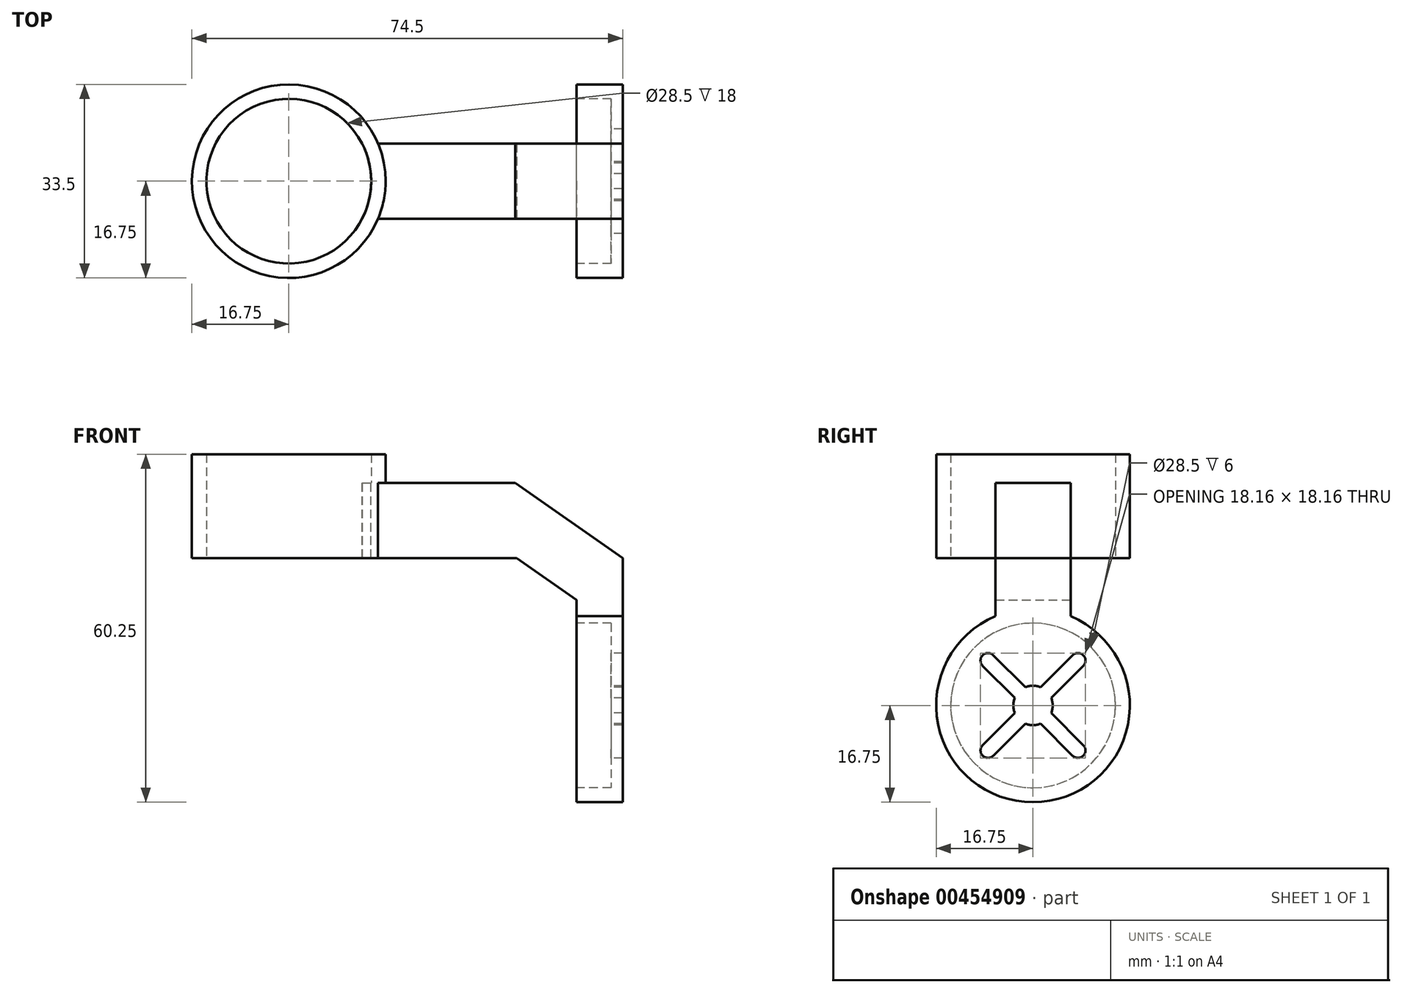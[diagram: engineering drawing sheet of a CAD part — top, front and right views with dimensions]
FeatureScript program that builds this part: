
annotation { "Feature Type Name" : "Feature", "Feature Type Description" : "" }
export const myFeature = defineFeature(function(context is Context, id is Id, definition is map)
    precondition{}
    {
        {
            var Q0;
            Q0=qCreatedBy(makeId("Top.planeOp"),FACE);
            var sketch = newSketch(context, id + "F0", { "sketchPlane" : qUnion([Q0])});
            skCircle(sketch, "E0", {"center": v(0, 0) * mm, "radius": 14.25 * mm});
            skCircle(sketch, "E1", {"center": v(0, 0) * mm, "radius": 16.75 * mm});
            skSolve(sketch);
        }
        {
            var Q0;
            Q0 = qSketchRegion(id + "F0", true);
            extrude(context, id + "F1", {"entities" : qUnion([Q0]), "depth" : 18 * mm});
        }
        {
            var Q0;
            Q0=qCreatedBy(makeId("Front.planeOp"),FACE);
            var sketch = newSketch(context, id + "F2", { "sketchPlane" : qUnion([Q0])});
            skLineSegment(sketch, "E2", {"start": v(39.05, 13) * mm, "end": v(39.15, 13) * mm});
            skLineSegment(sketch, "E3", {"start": v(44.75, 0) * mm, "end": v(44.75, -25.5) * mm});
            skPoint(sketch, "E4.orphan", {"position": v(57.75, 0) * mm});
            skLineSegment(sketch, "E5", {"start": v(57.75, 0) * mm, "end": v(39.15, 13) * mm});
            skLineSegment(sketch, "E6", {"start": v(44.75, -25.5) * mm, "end": v(57.75, -25.5) * mm});
            skLineSegment(sketch, "E7", {"start": v(57.75, -25.5) * mm, "end": v(57.75, 0) * mm});
            skPoint(sketch, "E8.orphan", {"position": v(57.75, 13) * mm});
            skLineSegment(sketch, "E9", {"start": v(39.05, 13) * mm, "end": v(9.9, 13) * mm});
            skLineSegment(sketch, "E10", {"start": v(9.9, 13) * mm, "end": v(9.9, 0) * mm});
            skLineSegment(sketch, "E11", {"start": v(44.75, 0) * mm, "end": v(9.9, 0) * mm});
            skSolve(sketch);
        }
        {
            var Q0;
            Q0 = qSketchRegion(id + "F2", true);
            extrude(context, id + "F3", {"entities" : qUnion([Q0]), "operationType" : NewBodyOperationType.ADD, "depth" : 13 / 2 * mm, "hasSecondDirection" : true, "secondDirectionOppositeDirection" : true, "secondDirectionDepth" : 6.5 * mm});
        }
        {
            var Q0;
            Q0=makeQuery(id+"F1.opExtrude","CAP_FACE",FACE,{"disambiguationData":[OSD([sQuery(id+"F0.wireOp",EDGE,"E0"),sQuery(id+"F0.wireOp",EDGE,"E1")])],"isStart":false});
            var sketch = newSketch(context, id + "F4", { "sketchPlane" : qUnion([Q0])});
            skCircle(sketch, "E12", {"center": v(0, 0) * mm, "radius": 14.24 * mm});
            skSolve(sketch);
        }
        {
            var Q0;
            Q0=makeQuery(id+"F4.imprint","IMPRINT",FACE,{"disambiguationData":[TD([[makeQuery(id+"F4.imprint","IMPRINT",EDGE,{"derivedFrom":sQuery(id+"F4.wireOp",EDGE,"E12")}),1.0]])]});
            extrude(context, id + "F5", {"entities" : qUnion([Q0]), "operationType" : NewBodyOperationType.REMOVE, "oppositeDirection" : true, "depth" : 25 * mm});
        }
        {
            var Q0;
            Q0=makeQuery(id+"F3.opExtrude","SWEPT_FACE",FACE,{"disambiguationData":[OSD([sQuery(id+"F2.wireOp",EDGE,"E7")])]});
            var sketch = newSketch(context, id + "F6", { "sketchPlane" : qUnion([Q0])});
            skCircle(sketch, "E13", {"center": v(0, -25.5) * mm, "radius": 16.75 * mm});
            skLineSegment(sketch, "E14", {"start": v(-16.75, 0) * mm, "end": v(-16.75, 18) * mm, "construction": true});
            skLineSegment(sketch, "E15", {"start": v(-16.75, 0) * mm, "end": v(-16.75, -40.9) * mm, "construction": true});
            skSolve(sketch);
        }
        {
            var Q0;
            Q0 = qSketchRegion(id + "F6", true);
            extrude(context, id + "F7", {"entities" : qUnion([Q0]), "operationType" : NewBodyOperationType.ADD, "oppositeDirection" : true, "depth" : 8 * mm});
        }
        {
            var Q0;
            {var subQ0=sQuery(id+"F2.wireOp",EDGE,"ThWkjC9a-3eqL-S6FN-Etdi-DtM8RTVKEJxe");var subQ1=sQuery(id+"F2.wireOp",EDGE,"YqEWwE9g-cm7q-8xzn-DUqV-dWurj4cPjtdj");var subQ2=sQuery(id+"F0.wireOp",EDGE,"E1");var subQ3=sQuery(id+"F2.wireOp",EDGE,"E9");var subQ4=sQuery(id+"F2.wireOp",EDGE,"E2");var subQ5=sQuery(id+"F2.wireOp",EDGE,"E3");var subQ6=sQuery(id+"F2.wireOp",EDGE,"E5");var subQ7=sQuery(id+"F2.wireOp",EDGE,"E6");var subQ8=sQuery(id+"F2.wireOp",EDGE,"E7");Q0=makeQuery(id+"F3.boolean.opBoolean","SPLIT",FACE,{"disambiguationData":[TD([makeQuery(id+"F1.opExtrude","SWEPT_FACE",FACE,{"disambiguationData":[OSD([subQ2])]})])],"derivedFrom":makeQuery(id+"F3.opExtrude","CAP_FACE",FACE,{"disambiguationData":[OSD([subQ1,subQ4,subQ5,subQ6,subQ7,subQ8,subQ3,sQuery(id+"F2.wireOp",EDGE,"E10"),subQ0])],"isStart":false})});}
            var sketch = newSketch(context, id + "F8", { "sketchPlane" : qUnion([Q0])});
            skLineSegment(sketch, "E16", {"start": v(49.75, -25.5) * mm, "end": v(44.75, -25.5) * mm});
            skLineSegment(sketch, "E17", {"start": v(44.75, -25.5) * mm, "end": v(44.75, -6.08) * mm});
            skLineSegment(sketch, "E18", {"start": v(44.75, -6.08) * mm, "end": v(49.75, -10.06) * mm});
            skLineSegment(sketch, "E19", {"start": v(49.75, -10.06) * mm, "end": v(49.75, -10.06) * mm});
            skSolve(sketch);
        }
        {
            var Q0;
            Q0 = qSketchRegion(id + "F8", true);
            var Q1;
            Q1=makeQuery(id+"F8.imprint","IMPRINT",FACE,{"disambiguationData":[TD([[makeQuery(id+"F8.imprint","IMPRINT",EDGE,{"derivedFrom":sQuery(id+"F8.wireOp",EDGE,"E16")}),1.0]])]});
            extrude(context, id + "F9", {"entities" : qUnion([Q0, Q1]), "operationType" : NewBodyOperationType.REMOVE, "oppositeDirection" : true, "depth" : 25 * mm});
        }
        {
            var Q0;
            {var subQ0=sQuery(id+"F6.wireOp",EDGE,"E13");Q0=makeQuery(id+"F9.boolean.opBoolean","MERGE",FACE,{"derivedFrom":[makeQuery(id+"F7.opExtrude","CAP_FACE",FACE,{"disambiguationData":[OSD([subQ0])],"isStart":false}),makeQuery(id+"F9.opExtrude","SWEPT_FACE",FACE,{"disambiguationData":[OSD([sQuery(id+"F2.wireOp",EDGE,"E2"),sQuery(id+"F2.wireOp",EDGE,"E3"),sQuery(id+"F2.wireOp",EDGE,"E5"),sQuery(id+"F2.wireOp",EDGE,"E6"),sQuery(id+"F2.wireOp",EDGE,"E7"),sQuery(id+"F2.wireOp",EDGE,"E9"),sQuery(id+"F2.wireOp",EDGE,"E10"),sQuery(id+"F2.wireOp",EDGE,"E11"),subQ0])]})]});}
            var sketch = newSketch(context, id + "F10", { "sketchPlane" : qUnion([Q0])});
            skCircle(sketch, "E20", {"center": v(0, -25.5) * mm, "radius": 14.25 * mm});
            skSolve(sketch);
        }
        {
            var Q0;
            Q0 = qSketchRegion(id + "F10", true);
            extrude(context, id + "F11", {"entities" : qUnion([Q0]), "operationType" : NewBodyOperationType.REMOVE, "oppositeDirection" : true, "depth" : 6 * mm, "hasSecondDirection" : true, "secondDirectionOppositeDirection" : false, "secondDirectionDepth" : 25 * mm});
        }
        {
            var Q0;
            {var subQ0=sQuery(id+"F2.wireOp",EDGE,"E9");var subQ1=sQuery(id+"F2.wireOp",EDGE,"E2");var subQ2=sQuery(id+"F0.wireOp",EDGE,"E1");var subQ3=sQuery(id+"F2.wireOp",EDGE,"E3");var subQ4=sQuery(id+"F2.wireOp",EDGE,"E5");var subQ5=sQuery(id+"F2.wireOp",EDGE,"E6");var subQ6=sQuery(id+"F2.wireOp",EDGE,"E7");var subQ7=sQuery(id+"F2.wireOp",EDGE,"E11");Q0=makeQuery(id+"F3.boolean.opBoolean","SPLIT",FACE,{"disambiguationData":[TD([makeQuery(id+"F1.opExtrude","SWEPT_FACE",FACE,{"disambiguationData":[OSD([subQ2])]})])],"derivedFrom":makeQuery(id+"F3.opExtrude","CAP_FACE",FACE,{"disambiguationData":[OSD([subQ1,subQ3,subQ4,subQ5,subQ6,subQ0,sQuery(id+"F2.wireOp",EDGE,"E10"),subQ7])],"isStart":false})});}
            var sketch = newSketch(context, id + "F12", { "sketchPlane" : qUnion([Q0])});
            skLineSegment(sketch, "E21", {"start": v(49.75, -7.23) * mm, "end": v(39.41, 0) * mm});
            skLineSegment(sketch, "E22", {"start": v(49.75, -7.23) * mm, "end": v(49.75, 0) * mm});
            skLineSegment(sketch, "E23", {"start": v(49.75, 0) * mm, "end": v(39.41, 0) * mm});
            skSolve(sketch);
        }
        {
            var Q0;
            Q0 = qSketchRegion(id + "F12", true);
            extrude(context, id + "F13", {"entities" : qUnion([Q0]), "operationType" : NewBodyOperationType.ADD, "oppositeDirection" : true, "depth" : 13 * mm});
        }
        {
            var Q0;
            {var subQ0=sQuery(id+"F2.wireOp",EDGE,"E9");var subQ1=sQuery(id+"F2.wireOp",EDGE,"E2");var subQ2=sQuery(id+"F0.wireOp",EDGE,"E1");var subQ3=sQuery(id+"F2.wireOp",EDGE,"E3");var subQ4=sQuery(id+"F2.wireOp",EDGE,"E5");var subQ5=sQuery(id+"F2.wireOp",EDGE,"E6");var subQ6=sQuery(id+"F2.wireOp",EDGE,"E7");var subQ7=sQuery(id+"F2.wireOp",EDGE,"E11");Q0=makeQuery(id+"F13.boolean.opBoolean","MERGE",FACE,{"derivedFrom":[makeQuery(id+"F3.boolean.opBoolean","SPLIT",FACE,{"disambiguationData":[TD([makeQuery(id+"F1.opExtrude","SWEPT_FACE",FACE,{"disambiguationData":[OSD([subQ2])]})])],"derivedFrom":makeQuery(id+"F3.opExtrude","CAP_FACE",FACE,{"disambiguationData":[OSD([subQ1,subQ3,subQ4,subQ5,subQ6,subQ0,sQuery(id+"F2.wireOp",EDGE,"E10"),subQ7])],"isStart":true})}),makeQuery(id+"F13.opExtrude","CAP_FACE",FACE,{"disambiguationData":[OSD([sQuery(id+"F12.wireOp",EDGE,"E21"),sQuery(id+"F12.wireOp",EDGE,"E22"),sQuery(id+"F12.wireOp",EDGE,"E23")])],"isStart":false})]});}
            var sketch = newSketch(context, id + "F14", { "sketchPlane" : qUnion([Q0])});
            skLineSegment(sketch, "E24", {"start": v(-49.75, -7.23) * mm, "end": v(-49.75, -10.06) * mm});
            skLineSegment(sketch, "E25", {"start": v(-49.75, -7.23) * mm, "end": v(-44.75, -3.73) * mm});
            skLineSegment(sketch, "E26", {"start": v(-49.75, -10.06) * mm, "end": v(-35.23, -9.45) * mm});
            skLineSegment(sketch, "E27", {"start": v(-35.23, -9.45) * mm, "end": v(-44.75, -3.73) * mm});
            skSolve(sketch);
        }
        {
            var Q0;
            Q0 = qSketchRegion(id + "F14", true);
            extrude(context, id + "F15", {"entities" : qUnion([Q0]), "operationType" : NewBodyOperationType.REMOVE, "oppositeDirection" : true, "depth" : 25 * mm});
        }
        {
            var Q0;
            Q0=makeQuery(id+"F11.boolean.opBoolean","COPY",FACE,{"derivedFrom":makeQuery(id+"F11.opExtrude","CAP_FACE",FACE,{"disambiguationData":[OSD([sQuery(id+"F10.wireOp",EDGE,"E20")])],"isStart":false})});
            var sketch = newSketch(context, id + "F16", { "sketchPlane" : qUnion([Q0])});
            skLineSegment(sketch, "E28", {"start": v(0, -25.5) * mm, "end": v(-14.25, -25.5) * mm, "construction": true});
            skPoint(sketch, "E29", {"position": v(-7.78, -17.72) * mm});
            skPoint(sketch, "E30", {"position": v(-2.23, -23.27) * mm});
            skArc(sketch, "E31.0.endCap", {"start": v(-8.7, -18.64) * mm, "mid": v(-8.7, -16.8) * mm, "end": v(-6.86, -16.8) * mm});
            skLineSegment(sketch, "E31.0.left", {"start": v(-3.15, -24.19) * mm, "end": v(-8.7, -18.64) * mm});
            skLineSegment(sketch, "E31.0.right", {"start": v(-1.31, -22.35) * mm, "end": v(-6.86, -16.8) * mm});
            skArc(sketch, "E32.MirrorCS", {"start": v(-6.86, -16.8) * mm, "mid": v(-8.7, -16.8) * mm, "end": v(-8.7, -18.64) * mm});
            skLineSegment(sketch, "E33.MirrorCS", {"start": v(0, -25.5) * mm, "end": v(-9.48, -25.5) * mm, "construction": true});
            skArc(sketch, "E34.MirrorCS", {"start": v(8.7, -18.64) * mm, "mid": v(8.7, -16.8) * mm, "end": v(6.86, -16.8) * mm});
            skLineSegment(sketch, "E35.MirrorCS", {"start": v(3.15, -24.19) * mm, "end": v(8.7, -18.64) * mm});
            skPoint(sketch, "E36.MirrorP", {"position": v(2.23, -23.27) * mm});
            skLineSegment(sketch, "E37.MirrorCS", {"start": v(1.31, -22.35) * mm, "end": v(6.86, -16.8) * mm});
            skArc(sketch, "E38.MirrorCS", {"start": v(6.86, -16.8) * mm, "mid": v(8.7, -16.8) * mm, "end": v(8.7, -18.64) * mm});
            skLineSegment(sketch, "E39.MirrorCS", {"start": v(3.15, -26.81) * mm, "end": v(8.7, -32.36) * mm});
            skLineSegment(sketch, "E40.MirrorCS", {"start": v(1.31, -28.65) * mm, "end": v(6.86, -34.2) * mm});
            skPoint(sketch, "E41.MirrorP", {"position": v(2.23, -27.73) * mm});
            skPoint(sketch, "E42.MirrorP", {"position": v(-2.23, -27.73) * mm});
            skPoint(sketch, "E43.MirrorP", {"position": v(7.78, -33.28) * mm});
            skArc(sketch, "E44.MirrorCS", {"start": v(6.86, -34.2) * mm, "mid": v(8.7, -34.2) * mm, "end": v(8.7, -32.36) * mm});
            skLineSegment(sketch, "E45.MirrorCS", {"start": v(-3.15, -26.81) * mm, "end": v(-8.7, -32.36) * mm});
            skPoint(sketch, "E46.MirrorP", {"position": v(-7.78, -33.28) * mm});
            skArc(sketch, "E47.MirrorCS", {"start": v(-8.7, -32.36) * mm, "mid": v(-8.7, -34.2) * mm, "end": v(-6.86, -34.2) * mm});
            skLineSegment(sketch, "E48.MirrorCS", {"start": v(-1.31, -28.65) * mm, "end": v(-6.86, -34.2) * mm});
            skArc(sketch, "E49.MirrorCS", {"start": v(8.7, -32.36) * mm, "mid": v(8.7, -34.2) * mm, "end": v(6.86, -34.2) * mm});
            skArc(sketch, "E50.MirrorCS", {"start": v(-6.86, -34.2) * mm, "mid": v(-8.7, -34.2) * mm, "end": v(-8.7, -32.36) * mm});
            skArc(sketch, "E51", {"start": v(-1.31, -28.65) * mm, "mid": v(0, -28.91) * mm, "end": v(1.31, -28.65) * mm});
            skArc(sketch, "E52.trimOffspring", {"start": v(1.31, -22.35) * mm, "mid": v(0, -22.09) * mm, "end": v(-1.31, -22.35) * mm});
            skArc(sketch, "E53.trimOffspring", {"start": v(-3.15, -24.19) * mm, "mid": v(-3.41, -25.5) * mm, "end": v(-3.15, -26.81) * mm});
            skArc(sketch, "E54.trimOffspring", {"start": v(3.15, -26.81) * mm, "mid": v(3.41, -25.5) * mm, "end": v(3.15, -24.19) * mm});
            skSolve(sketch);
        }
        {
            var Q0;
            Q0 = qSketchRegion(id + "F16", true);
            extrude(context, id + "F17", {"entities" : qUnion([Q0]), "operationType" : NewBodyOperationType.REMOVE, "oppositeDirection" : true, "depth" : 25 * mm});
        }
    });
